# Revit family: HRF-SER
name_source: partatom
category: Plumbing Fixtures
units: mm (PartAtom-declared; Revit-internal decimal feet)

## family parameters
Always vertical = Yes
Cut with Voids When Loaded = No
OmniClass Number = 23.45.00.00
OmniClass Title = Sanitary, Laundry, and Cleaning Equipment
Part Type = Normal
Room Calculation Point = No
Round Connector Dimension = Use Radius
Shared = No
Work Plane-Based = No

## types (3) — shared parameters
Activation = Pushbutton
Back Panel = Yes
Bubbler = Double Bubbler
Bubbler Material = Metal - Steel - Stainless - Chrome
Button Material = Metal - Steel - Stainless - Chrome
CW Connection = Yes
Chiller = Yes
Chiller Option = Yes
Cooler Depth = 1' - 6 5/8"
Cooler Separation = 0' - 6 5/8"
Cooler Width = 1' - 0 1/8"
Description = Water Cooler
Dispenser Height = 2' - 9"
Filter = **ACC (HWF172)
HW Connection = No
Lower Cooler Rim Height = 2' - 9 1/2"
Lower Orifice Height = 2' - 11 1/8"
Manufacturer = halseytaylor
Model = HRFG-SEBP FTN
Mounting Plate = Incl Suface Mtg Plate
Orifice to Rim = 0' - 1 5/8"
Rim to Dispenser = 0' - 6 1/2"
Sanitary Service Size Radius = 0' - 0 5/8"
Type = Bi-level
URL = http://www.halseytaylor.com
Upper Cooler Depth = 1' - 0 7/8"
Upper Cooler Rim Height = 3' - 3 1/2"
Upper Orifice Height = 3' - 5 1/8"
Upper Rim Height = 3' - 3 1/2"
Vent Connection = No
Version = 1.0.0.0
Voltage = 115 V
Volts/Hertz = 115V/60Hz
Wall Plate Material = Metal - Steel - Stainless - Chrome
Waste Connection = Yes
Water Service Flow = 0 GPM
Water Service Flow Out = 0 GPM
Water Service Size Radius = 0' - 0 1/4"

## per-type parameters (varying)
| type | Basin Material | Sanitary Connector Description | Water Connector Description | Water Out Connection Description |
| HRFG-SER BLK BASIN | BLK Marblyte |  |  |  |
| HRF-SER | Metal - Steel - Stainless - Chrome | 1 1/4" O.D. | 3/8" O.D. | 1/4" O.D. |
| HRFG-SER GRY BASIN | GRY Marblyte |  |  |  |

## geometry (parser evidence)
native form markers: Sweep x9
no freeform markers — native parametric forms only
